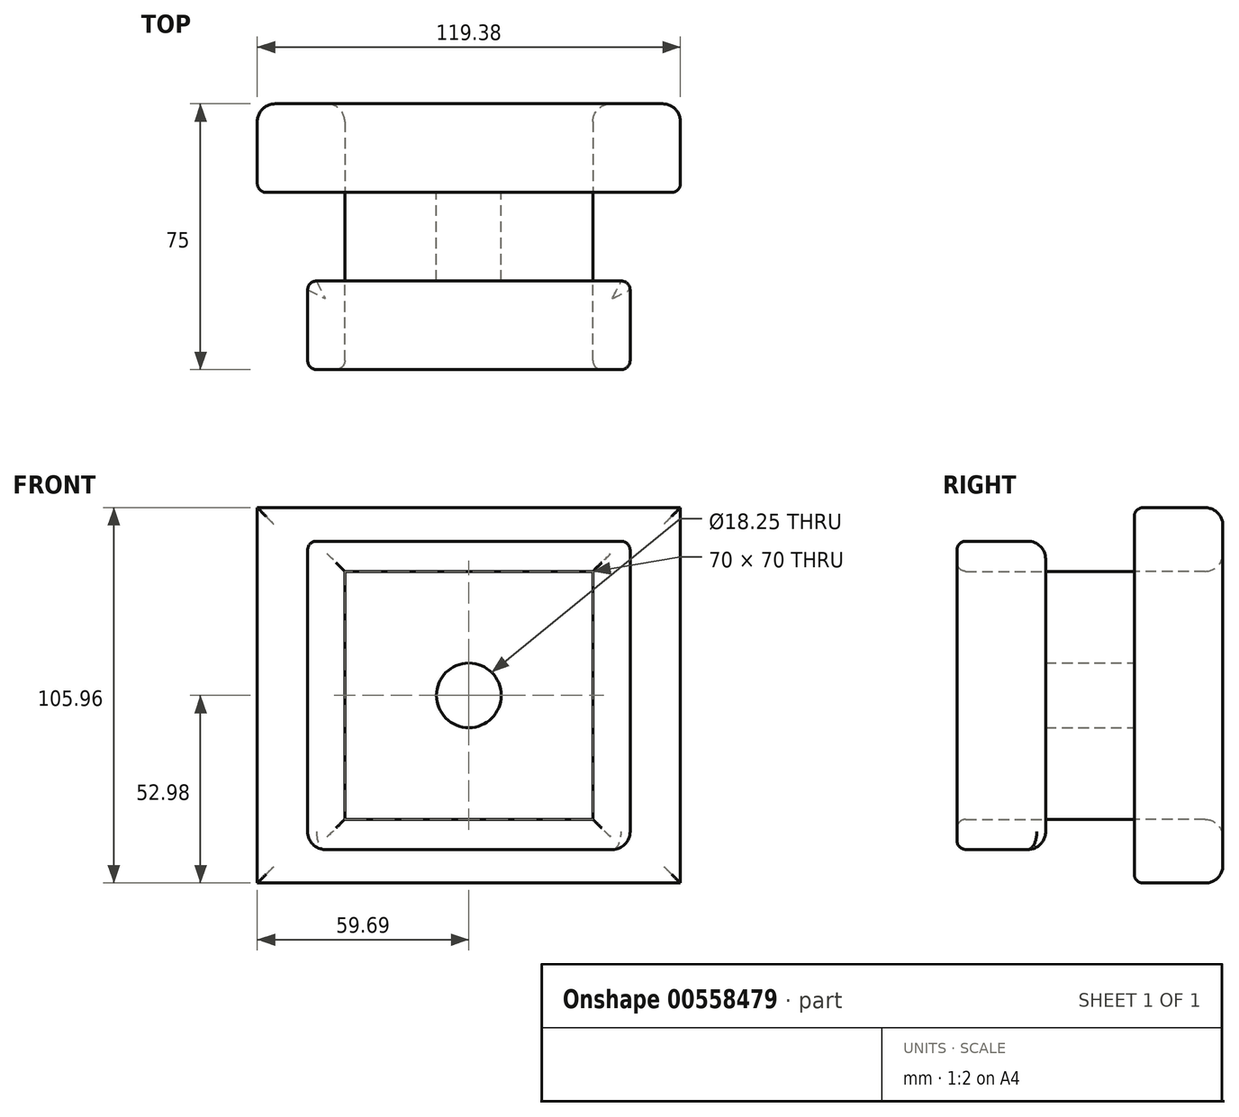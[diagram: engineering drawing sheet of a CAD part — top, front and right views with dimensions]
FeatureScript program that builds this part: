
annotation { "Feature Type Name" : "Feature", "Feature Type Description" : "" }
export const myFeature = defineFeature(function(context is Context, id is Id, definition is map)
    precondition{}
    {
        {
            var Q0;
            Q0=qCreatedBy(makeId("Front.planeOp"),FACE);
            var sketch = newSketch(context, id + "F0", { "sketchPlane" : qUnion([Q0])});
            skLineSegment(sketch, "E0.bottom", {"start": v(-35, 35) * mm, "end": v(35, 35) * mm});
            skLineSegment(sketch, "E0.top", {"start": v(-35, -35) * mm, "end": v(35, -35) * mm});
            skLineSegment(sketch, "E0.left", {"start": v(-35, 35) * mm, "end": v(-35, -35) * mm});
            skLineSegment(sketch, "E0.right", {"start": v(35, 35) * mm, "end": v(35, -35) * mm});
            skPoint(sketch, "E0.middle", {"position": v(0, 0) * mm});
            skSolve(sketch);
        }
        {
            var Q0;
            Q0=makeQuery(id+"F0.imprint","IMPRINT",FACE,{"disambiguationData":[TD([[makeQuery(id+"F0.imprint","IMPRINT",EDGE,{"derivedFrom":sQuery(id+"F0.wireOp",EDGE,"E0.bottom")}),-1.0]])]});
            extrude(context, id + "F1", {"entities" : qUnion([Q0]), "depth" : 25 * mm, "offsetDistance" : 25 * mm});
        }
        {
            var Q0;
            Q0=makeQuery(id+"F1.opExtrude","CAP_FACE",FACE,{"disambiguationData":[OSD([sQuery(id+"F0.wireOp",EDGE,"E0.bottom"),sQuery(id+"F0.wireOp",EDGE,"E0.top"),sQuery(id+"F0.wireOp",EDGE,"E0.left"),sQuery(id+"F0.wireOp",EDGE,"E0.right")])],"isStart":false});
            var sketch = newSketch(context, id + "F2", { "sketchPlane" : qUnion([Q0])});
            skLineSegment(sketch, "E1.bottom", {"start": v(45.49, 43.52) * mm, "end": v(-45.49, 43.52) * mm});
            skLineSegment(sketch, "E1.top", {"start": v(45.49, -43.52) * mm, "end": v(-45.49, -43.52) * mm});
            skLineSegment(sketch, "E1.left", {"start": v(45.49, 43.52) * mm, "end": v(45.49, -43.52) * mm});
            skLineSegment(sketch, "E1.right", {"start": v(-45.49, 43.52) * mm, "end": v(-45.49, -43.52) * mm});
            skPoint(sketch, "E1.middle", {"position": v(0, 0) * mm});
            skSolve(sketch);
        }
        {
            var Q0;
            Q0=makeQuery(id+"F2.imprint","IMPRINT",FACE,{"disambiguationData":[TD([[makeQuery(id+"F2.imprint","IMPRINT",EDGE,{"derivedFrom":sQuery(id+"F2.wireOp",EDGE,"E1.bottom")}),1.0]])]});
            extrude(context, id + "F3", {"entities" : qUnion([Q0]), "depth" : 25 * mm, "offsetDistance" : 25 * mm});
        }
        {
            var Q0;
            Q0=makeQuery(id+"F1.opExtrude","CAP_FACE",FACE,{"disambiguationData":[OSD([sQuery(id+"F0.wireOp",EDGE,"E0.bottom"),sQuery(id+"F0.wireOp",EDGE,"E0.top"),sQuery(id+"F0.wireOp",EDGE,"E0.left"),sQuery(id+"F0.wireOp",EDGE,"E0.right")])],"isStart":true});
            var sketch = newSketch(context, id + "F4", { "sketchPlane" : qUnion([Q0])});
            skLineSegment(sketch, "E2.bottom", {"start": v(59.69, 52.98) * mm, "end": v(-59.69, 52.98) * mm});
            skLineSegment(sketch, "E2.top", {"start": v(59.69, -52.98) * mm, "end": v(-59.69, -52.98) * mm});
            skLineSegment(sketch, "E2.left", {"start": v(59.69, 52.98) * mm, "end": v(59.69, -52.98) * mm});
            skLineSegment(sketch, "E2.right", {"start": v(-59.69, 52.98) * mm, "end": v(-59.69, -52.98) * mm});
            skPoint(sketch, "E2.middle", {"position": v(0, 0) * mm});
            skSolve(sketch);
        }
        {
            var Q0;
            Q0=makeQuery(id+"F4.imprint","IMPRINT",FACE,{"disambiguationData":[TD([[makeQuery(id+"F4.imprint","IMPRINT",EDGE,{"derivedFrom":sQuery(id+"F4.wireOp",EDGE,"E2.bottom")}),1.0]])]});
            extrude(context, id + "F5", {"entities" : qUnion([Q0]), "depth" : 25 * mm, "offsetDistance" : 25 * mm});
        }
        {
            var Q0;
            Q0=makeQuery(id+"F1.opExtrude","CAP_FACE",FACE,{"disambiguationData":[OSD([sQuery(id+"F0.wireOp",EDGE,"E0.bottom"),sQuery(id+"F0.wireOp",EDGE,"E0.top"),sQuery(id+"F0.wireOp",EDGE,"E0.left"),sQuery(id+"F0.wireOp",EDGE,"E0.right")])],"isStart":true});
            var sketch = newSketch(context, id + "F6", { "sketchPlane" : qUnion([Q0])});
            skCircle(sketch, "E3", {"center": v(0, 0) * mm, "radius": 9.12 * mm});
            skSolve(sketch);
        }
        {
            var Q0;
            Q0=makeQuery(id+"F6.imprint","IMPRINT",FACE,{"disambiguationData":[TD([[makeQuery(id+"F6.imprint","IMPRINT",EDGE,{"derivedFrom":sQuery(id+"F6.wireOp",EDGE,"E3")}),1.0]])]});
            extrude(context, id + "F7", {"entities" : qUnion([Q0]), "operationType" : NewBodyOperationType.REMOVE, "oppositeDirection" : true, "depth" : 25 * mm, "offsetDistance" : 25 * mm});
        }
        {
            var Q0;
            Q0=makeQuery(id+"F7.boolean.opBoolean","COPY",EDGE,{"derivedFrom":makeQuery(id+"F7.opExtrude","CAP_EDGE",EDGE,{"disambiguationData":[OSD([sQuery(id+"F6.wireOp",EDGE,"E3")])],"isStart":false})});
            var Q1;
            Q1=makeQuery(id+"F3.opExtrude","CAP_EDGE",EDGE,{"disambiguationData":[OSD([sQuery(id+"F0.wireOp",EDGE,"E0.left")])],"isStart":false});
            var Q2;
            Q2=makeQuery(id+"F3.opExtrude","CAP_EDGE",EDGE,{"disambiguationData":[OSD([sQuery(id+"F0.wireOp",EDGE,"E0.bottom")])],"isStart":false});
            var Q3;
            Q3=makeQuery(id+"F3.opExtrude","CAP_EDGE",EDGE,{"disambiguationData":[OSD([sQuery(id+"F0.wireOp",EDGE,"E0.right")])],"isStart":false});
            var Q4;
            Q4=makeQuery(id+"F3.opExtrude","CAP_EDGE",EDGE,{"disambiguationData":[OSD([sQuery(id+"F0.wireOp",EDGE,"E0.top")])],"isStart":false});
            var Q5;
            Q5=makeQuery(id+"F3.opExtrude","CAP_EDGE",EDGE,{"disambiguationData":[OSD([sQuery(id+"F2.wireOp",EDGE,"E1.right")])],"isStart":false});
            var Q6;
            Q6=makeQuery(id+"F3.opExtrude","CAP_EDGE",EDGE,{"disambiguationData":[OSD([sQuery(id+"F2.wireOp",EDGE,"E1.bottom")])],"isStart":false});
            var Q7;
            Q7=makeQuery(id+"F3.opExtrude","CAP_EDGE",EDGE,{"disambiguationData":[OSD([sQuery(id+"F2.wireOp",EDGE,"E1.left")])],"isStart":false});
            var Q8;
            Q8=makeQuery(id+"F3.opExtrude","CAP_EDGE",EDGE,{"disambiguationData":[OSD([sQuery(id+"F2.wireOp",EDGE,"E1.top")])],"isStart":false});
            var Q9;
            Q9=makeQuery(id+"F5.opExtrude","CAP_EDGE",EDGE,{"disambiguationData":[OSD([sQuery(id+"F4.wireOp",EDGE,"E2.left")])],"isStart":true});
            var Q10;
            Q10=makeQuery(id+"F5.opExtrude","CAP_EDGE",EDGE,{"disambiguationData":[OSD([sQuery(id+"F4.wireOp",EDGE,"E2.bottom")])],"isStart":true});
            var Q11;
            Q11=makeQuery(id+"F5.opExtrude","CAP_EDGE",EDGE,{"disambiguationData":[OSD([sQuery(id+"F4.wireOp",EDGE,"E2.right")])],"isStart":true});
            var Q12;
            Q12=makeQuery(id+"F5.opExtrude","CAP_EDGE",EDGE,{"disambiguationData":[OSD([sQuery(id+"F4.wireOp",EDGE,"E2.top")])],"isStart":true});
            fillet(context, id + "F8", {"entities" : qUnion([Q0, Q1, Q2, Q3, Q4, Q5, Q6, Q7, Q8, Q9, Q10, Q11, Q12]), "radius" : 2.5 * mm, "tangentPropagation" : true, "allowEdgeOverflow" : false});
        }
        {
            var Q0;
            Q0=makeQuery(id+"F3.opExtrude","CAP_EDGE",EDGE,{"disambiguationData":[OSD([sQuery(id+"F2.wireOp",EDGE,"E1.bottom")])],"isStart":true});
            fillet(context, id + "F9", {"entities" : qUnion([Q0]), "radius" : 5 * mm, "tangentPropagation" : true, "allowEdgeOverflow" : false});
        }
        {
            var Q0;
            Q0=makeQuery(id+"F3.opExtrude","CAP_EDGE",EDGE,{"disambiguationData":[OSD([sQuery(id+"F2.wireOp",EDGE,"E1.left")])],"isStart":true});
            var Q1;
            Q1=makeQuery(id+"F9.opFillet","BLEND_FACE",FACE,{"disambiguationData":[OSD([sQuery(id+"F2.wireOp",EDGE,"E1.bottom")])]});
            fillet(context, id + "F10", {"entities" : qUnion([Q0, Q1]), "radius" : 2.5 * mm, "tangentPropagation" : true, "allowEdgeOverflow" : false});
        }
        {
            var Q0;
            Q0=makeQuery(id+"F10.opFillet","BLEND_FACE",FACE,{"disambiguationData":[OSD([sQuery(id+"F2.wireOp",EDGE,"E1.left")])]});
            var Q1;
            {var subQ0=sQuery(id+"F2.wireOp",EDGE,"E1.top");Q1=makeQuery(id+"F8.opFillet","BLEND_EDGE",EDGE,{"blendedFrom":[makeQuery(id+"F3.opExtrude","CAP_EDGE",EDGE,{"disambiguationData":[OSD([subQ0])],"isStart":false}),makeQuery(id+"F3.opExtrude","CAP_FACE",FACE,{"disambiguationData":[OSD([sQuery(id+"F0.wireOp",EDGE,"E0.bottom"),sQuery(id+"F0.wireOp",EDGE,"E0.top"),sQuery(id+"F0.wireOp",EDGE,"E0.left"),sQuery(id+"F0.wireOp",EDGE,"E0.right"),sQuery(id+"F2.wireOp",EDGE,"E1.bottom"),subQ0,sQuery(id+"F2.wireOp",EDGE,"E1.left"),sQuery(id+"F2.wireOp",EDGE,"E1.right")])],"isStart":false})],"blendedInto":[makeQuery(id+"F3.opExtrude","CAP_FACE",FACE,{"disambiguationData":[OSD([sQuery(id+"F0.wireOp",EDGE,"E0.bottom"),sQuery(id+"F0.wireOp",EDGE,"E0.top"),sQuery(id+"F0.wireOp",EDGE,"E0.left"),sQuery(id+"F0.wireOp",EDGE,"E0.right"),sQuery(id+"F2.wireOp",EDGE,"E1.bottom"),subQ0,sQuery(id+"F2.wireOp",EDGE,"E1.left"),sQuery(id+"F2.wireOp",EDGE,"E1.right")])],"isStart":false})]});}
            var Q2;
            Q2=makeQuery(id+"F5.opExtrude","CAP_EDGE",EDGE,{"disambiguationData":[OSD([sQuery(id+"F4.wireOp",EDGE,"E2.right")])],"isStart":false});
            var Q3;
            Q3=makeQuery(id+"F5.opExtrude","CAP_EDGE",EDGE,{"disambiguationData":[OSD([sQuery(id+"F4.wireOp",EDGE,"E2.top")])],"isStart":false});
            var Q4;
            Q4=makeQuery(id+"F5.opExtrude","CAP_EDGE",EDGE,{"disambiguationData":[OSD([sQuery(id+"F4.wireOp",EDGE,"E2.left")])],"isStart":false});
            var Q5;
            Q5=makeQuery(id+"F5.opExtrude","CAP_EDGE",EDGE,{"disambiguationData":[OSD([sQuery(id+"F0.wireOp",EDGE,"E0.left")])],"isStart":false});
            var Q6;
            Q6=makeQuery(id+"F5.opExtrude","CAP_EDGE",EDGE,{"disambiguationData":[OSD([sQuery(id+"F0.wireOp",EDGE,"E0.top")])],"isStart":false});
            var Q7;
            Q7=makeQuery(id+"F5.opExtrude","CAP_FACE",FACE,{"disambiguationData":[OSD([sQuery(id+"F0.wireOp",EDGE,"E0.bottom"),sQuery(id+"F0.wireOp",EDGE,"E0.top"),sQuery(id+"F0.wireOp",EDGE,"E0.left"),sQuery(id+"F0.wireOp",EDGE,"E0.right"),sQuery(id+"F4.wireOp",EDGE,"E2.bottom"),sQuery(id+"F4.wireOp",EDGE,"E2.top"),sQuery(id+"F4.wireOp",EDGE,"E2.left"),sQuery(id+"F4.wireOp",EDGE,"E2.right")])],"isStart":false});
            var Q8;
            Q8=makeQuery(id+"F5.opExtrude","CAP_EDGE",EDGE,{"disambiguationData":[OSD([sQuery(id+"F0.wireOp",EDGE,"E0.bottom")])],"isStart":false});
            var Q9;
            Q9=makeQuery(id+"F7.boolean.opBoolean","COPY",EDGE,{"derivedFrom":makeQuery(id+"F7.opExtrude","CAP_EDGE",EDGE,{"disambiguationData":[OSD([sQuery(id+"F6.wireOp",EDGE,"E3")])],"isStart":true})});
            fillet(context, id + "F11", {"entities" : qUnion([Q0, Q1, Q2, Q3, Q4, Q5, Q6, Q7, Q8, Q9]), "radius" : 5 * mm, "tangentPropagation" : true, "allowEdgeOverflow" : false});
        }
    });
